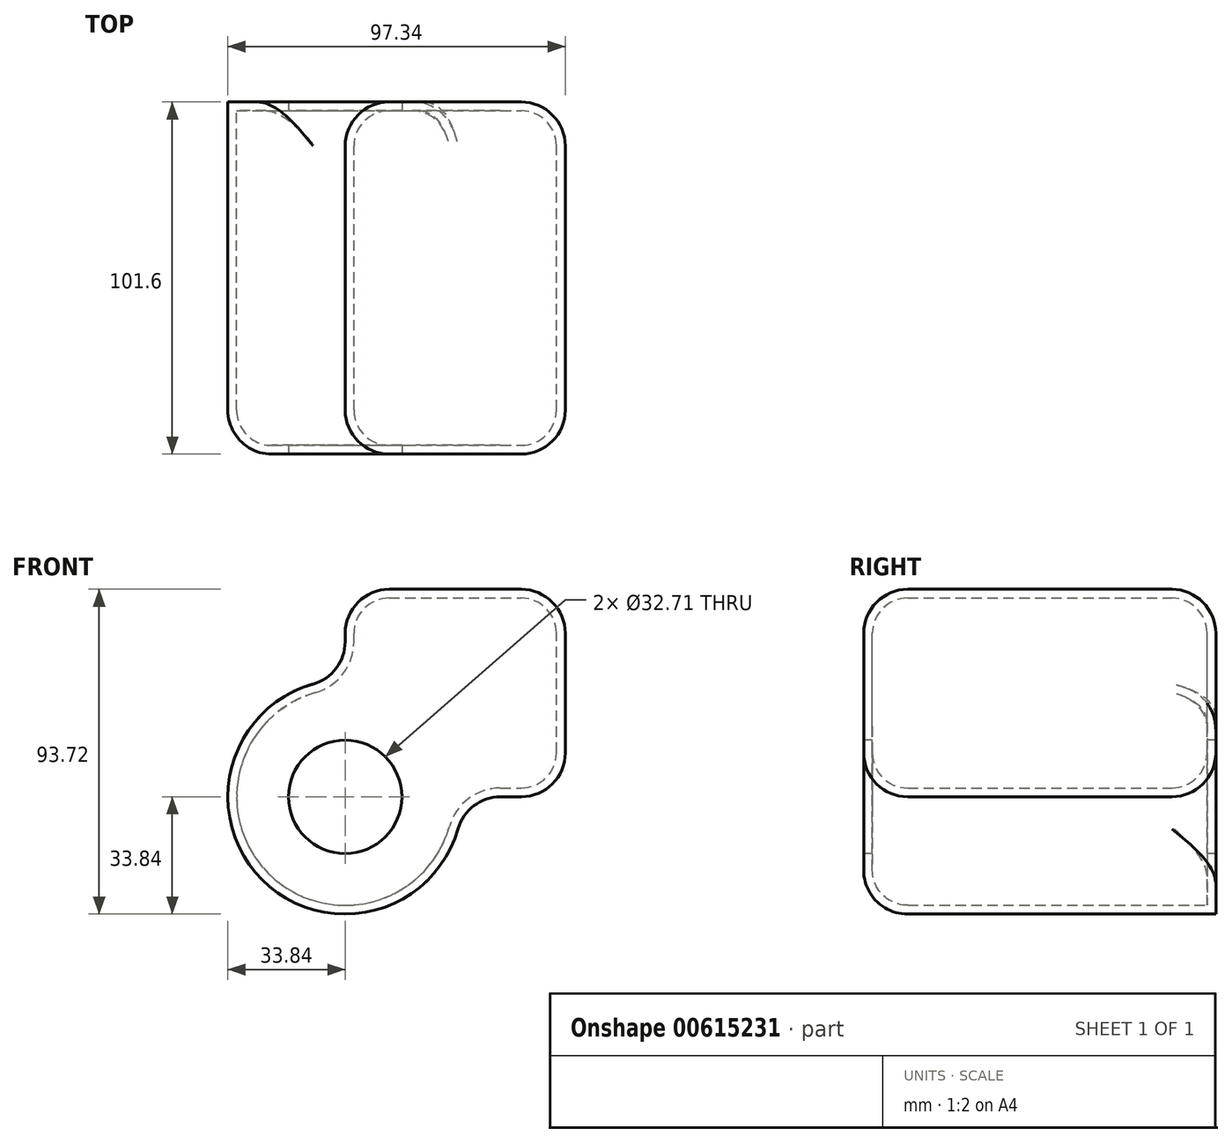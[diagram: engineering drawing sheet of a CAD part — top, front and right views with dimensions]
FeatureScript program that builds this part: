
annotation { "Feature Type Name" : "Feature", "Feature Type Description" : "" }
export const myFeature = defineFeature(function(context is Context, id is Id, definition is map)
    precondition{}
    {
        {
            var Q0;
            Q0=qCreatedBy(makeId("Front.planeOp"),FACE);
            var sketch = newSketch(context, id + "F0", { "sketchPlane" : qUnion([Q0])});
            skLineSegment(sketch, "E0.bottom", {"start": v(33.84, 0) * mm, "end": v(63.5, 0) * mm});
            skLineSegment(sketch, "E0.top", {"start": v(0, 59.88) * mm, "end": v(63.5, 59.88) * mm});
            skLineSegment(sketch, "E0.left", {"start": v(0, 33.84) * mm, "end": v(0, 59.88) * mm});
            skLineSegment(sketch, "E0.right", {"start": v(63.5, 0) * mm, "end": v(63.5, 59.88) * mm});
            skArc(sketch, "E1", {"start": v(0, 33.84) * mm, "mid": v(-23.93, -23.93) * mm, "end": v(33.84, 0) * mm});
            skSolve(sketch);
        }
        {
            var Q0;
            Q0 = qSketchRegion(id + "F0", true);
            extrude(context, id + "F1", {"entities" : qUnion([Q0]), "depth" : 101.6 * mm, "offsetDistance" : 25.4 * mm});
        }
        {
            var Q0;
            Q0=makeQuery(id+"F1.opExtrude","SWEPT_EDGE",EDGE,{"disambiguationData":[OSD([sQuery(id+"F0.wireOp",EDGE,"E0.top"),sQuery(id+"F0.wireOp",EDGE,"E0.right")])]});
            var Q1;
            Q1=makeQuery(id+"F1.opExtrude","SWEPT_FACE",FACE,{"disambiguationData":[OSD([sQuery(id+"F0.wireOp",EDGE,"E0.bottom")])]});
            var Q2;
            Q2=makeQuery(id+"F1.opExtrude","CAP_EDGE",EDGE,{"disambiguationData":[OSD([sQuery(id+"F0.wireOp",EDGE,"E0.right")])],"isStart":false});
            var Q3;
            Q3=makeQuery(id+"F1.opExtrude","CAP_FACE",FACE,{"disambiguationData":[OSD([sQuery(id+"F0.wireOp",EDGE,"E0.bottom"),sQuery(id+"F0.wireOp",EDGE,"E0.top"),sQuery(id+"F0.wireOp",EDGE,"E0.left"),sQuery(id+"F0.wireOp",EDGE,"E0.right"),sQuery(id+"F0.wireOp",EDGE,"E1")])],"isStart":false});
            var Q4;
            Q4=makeQuery(id+"F1.opExtrude","CAP_EDGE",EDGE,{"disambiguationData":[OSD([sQuery(id+"F0.wireOp",EDGE,"E0.right")])],"isStart":true});
            var Q5;
            Q5=makeQuery(id+"F1.opExtrude","CAP_EDGE",EDGE,{"disambiguationData":[OSD([sQuery(id+"F0.wireOp",EDGE,"E0.top")])],"isStart":true});
            var Q6;
            Q6=makeQuery(id+"F1.opExtrude","SWEPT_EDGE",EDGE,{"disambiguationData":[OSD([sQuery(id+"F0.wireOp",EDGE,"E0.top"),sQuery(id+"F0.wireOp",EDGE,"E0.left")])]});
            var Q7;
            Q7=makeQuery(id+"F1.opExtrude","CAP_EDGE",EDGE,{"disambiguationData":[OSD([sQuery(id+"F0.wireOp",EDGE,"E0.left")])],"isStart":true});
            var Q8;
            Q8=makeQuery(id+"F1.opExtrude","SWEPT_EDGE",EDGE,{"disambiguationData":[OSD([sQuery(id+"F0.wireOp",EDGE,"E0.left"),sQuery(id+"F0.wireOp",EDGE,"E1")])]});
            fillet(context, id + "F2", {"entities" : qUnion([Q0, Q1, Q2, Q3, Q4, Q5, Q6, Q7, Q8]), "radius" : 12.7 * mm, "tangentPropagation" : true, "allowEdgeOverflow" : false});
        }
        {
            var Q0;
            Q0=makeQuery(id+"F1.opExtrude","CAP_FACE",FACE,{"disambiguationData":[OSD([sQuery(id+"F0.wireOp",EDGE,"E0.bottom"),sQuery(id+"F0.wireOp",EDGE,"E0.top"),sQuery(id+"F0.wireOp",EDGE,"E0.left"),sQuery(id+"F0.wireOp",EDGE,"E0.right"),sQuery(id+"F0.wireOp",EDGE,"E1")])],"isStart":false});
            var sketch = newSketch(context, id + "F3", { "sketchPlane" : qUnion([Q0])});
            skCircle(sketch, "E2", {"center": v(0, 0) * mm, "radius": 16.35 * mm});
            skSolve(sketch);
        }
        {
            var Q0;
            Q0 = qSketchRegion(id + "F3", true);
            extrude(context, id + "F4", {"entities" : qUnion([Q0]), "operationType" : NewBodyOperationType.REMOVE, "endBound" : BoundingType.THROUGH_ALL, "oppositeDirection" : true, "depth" : 25.4 * mm, "offsetDistance" : 25.4 * mm});
        }
        {
            var Q0;
            Q0=makeQuery(id+"F4.boolean.opBoolean","COPY",FACE,{"derivedFrom":makeQuery(id+"F4.opExtrude","SWEPT_FACE",FACE,{"disambiguationData":[OSD([sQuery(id+"F3.wireOp",EDGE,"E2")])]})});
            shell(context, id + "F5", {"entities" : qUnion([Q0]), "thickness" : 2.54 * mm});
        }
    });
